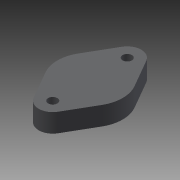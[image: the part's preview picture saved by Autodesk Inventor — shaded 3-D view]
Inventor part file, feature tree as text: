
AUTODESK INVENTOR PART (.ipt)
format: ipt  version: 2013 (Build 170138000, 138)  size: 91,136 bytes
history: native  units: mm
features: extrude x1, sketch x1
ambient origin geometry x8: Origin, YZ Plane, XZ Plane, XY Plane, X Axis, Y Axis, Z Axis, Center Point
bodies: Solid1 (feature_tree)
feature tree (2):
  extrude  "Extrusion1"  [1 undecoded]
  sketch  "Sketch1"  dims[d0=6.0mm d1=0.0mm]
note: 1 required parameter value undecoded (feature->parameter linkage not recoverable at this tier; creation-order binding heuristic only, values carry confidence <= 0.55)
